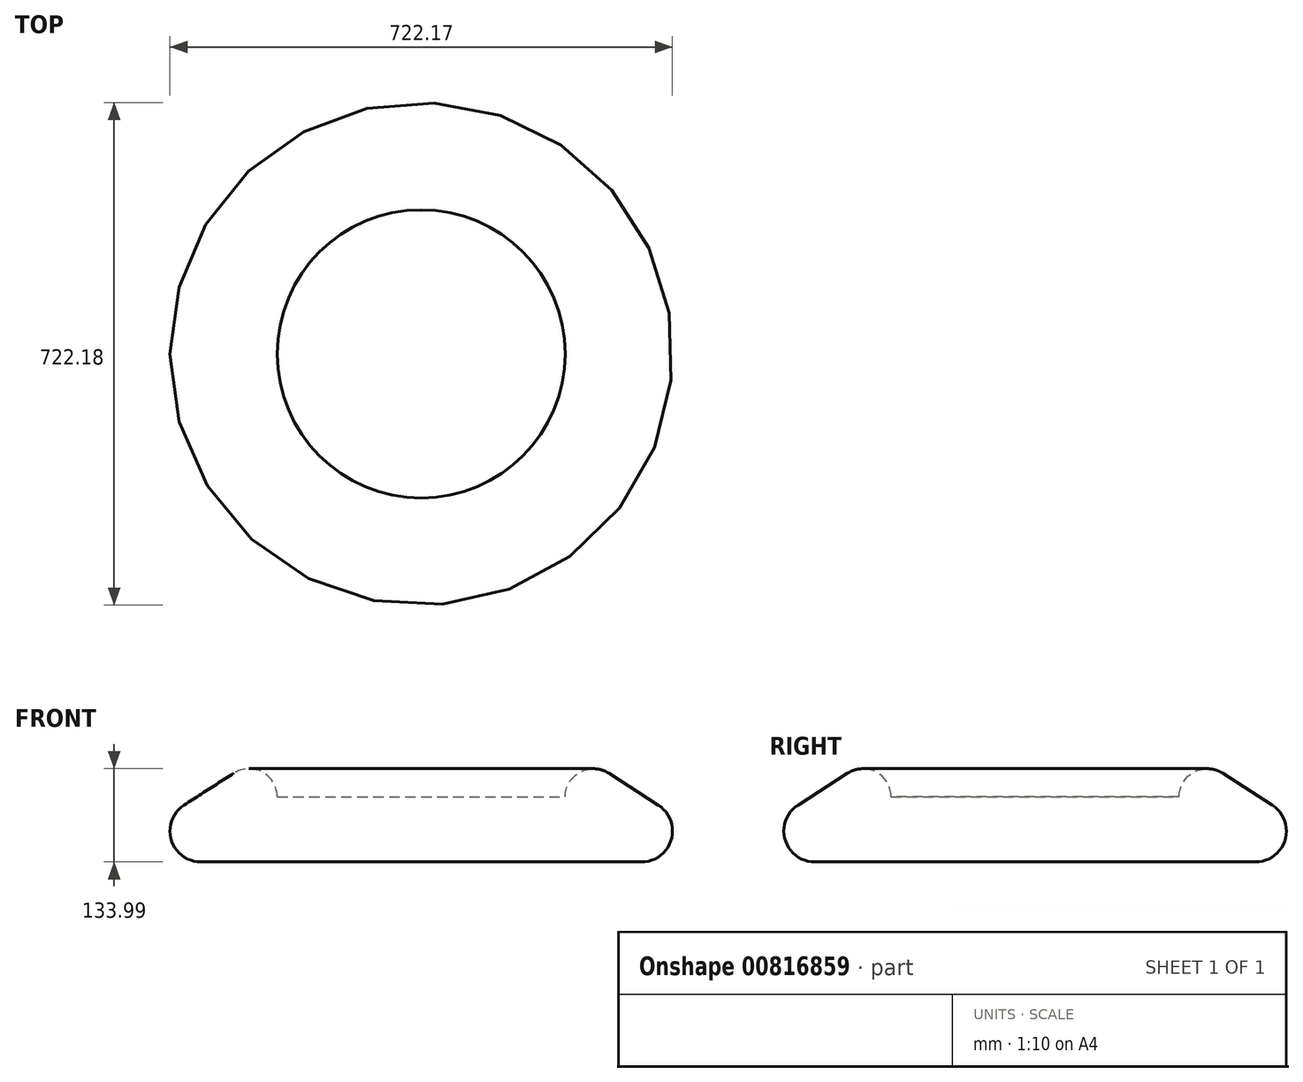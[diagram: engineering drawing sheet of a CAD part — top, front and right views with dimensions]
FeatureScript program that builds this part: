
annotation { "Feature Type Name" : "Feature", "Feature Type Description" : "" }
export const myFeature = defineFeature(function(context is Context, id is Id, definition is map)
    precondition{}
    {
        {
            var Q0;
            Q0=qCreatedBy(makeId("Front.planeOp"),FACE);
            var sketch = newSketch(context, id + "F0", { "sketchPlane" : qUnion([Q0])});
            skArc(sketch, "E0", {"start": v(40.53, 0) * mm, "mid": v(19.42, 35.58) * mm, "end": v(-21.93, 34.1) * mm});
            skArc(sketch, "E1", {"start": v(-93.26, -11.78) * mm, "mid": v(-111.82, -61.6) * mm, "end": v(-69.26, -93.46) * mm});
            skLineSegment(sketch, "E2", {"start": v(-69.26, -93.46) * mm, "end": v(247.46, -93.46) * mm});
            skLineSegment(sketch, "E3", {"start": v(247.46, -93.46) * mm, "end": v(247.46, 0) * mm});
            skLineSegment(sketch, "E4", {"start": v(247.46, 0) * mm, "end": v(40.53, 0) * mm});
            skLineSegment(sketch, "E5", {"start": v(-93.26, -11.78) * mm, "end": v(-21.93, 34.1) * mm});
            skSolve(sketch);
        }
        {
            var Q0;
            Q0=makeQuery(id+"F0.imprint","IMPRINT",FACE,{"disambiguationData":[TD([[makeQuery(id+"F0.imprint","IMPRINT",EDGE,{"derivedFrom":sQuery(id+"F0.wireOp",EDGE,"E0")}),1.0]])]});
            var Q1;
            Q1=sQuery(id+"F0.wireOp",EDGE,"E3");
            revolve(context, id + "F1", {"surfaceOperationType" : NewSurfaceOperationType.NEW, "entities" : qUnion([Q0]), "axis" : qUnion([Q1]), "revolveType" : RevolveType.FULL});
        }
    });
